# Revit family: M186140xx--Sanitary_Shower-screens_Roca_VICTORIA-L2-E-1400-Front-shower-enclosure-with-1-sliding-door-+-1-fixed-panel
name_source: partatom
category: Specialty Equipment
units: mm (PartAtom-declared; Revit-internal decimal feet)

## family parameters
Always vertical = No
Cut with Voids When Loaded = No
OmniClass Number = 23.31.17.25
Part Type = Normal
Room Calculation Point = No
Round Connector Dimension = Use Diameter
Shared = No
Work Plane-Based = No

## types (1)
- VICTORIA L2-E 1400 - Front shower enclosure with 1 sliding door + 1 fixed panel
    Always visible = Yes
    BIMobject category = Shower screens
    Design country = Spain
    Edition number = 1
    Frame material = Roca - VICTORIA - Polished silver
    IFC Classification = Wall
    Installation instructions = http://www.export.roca.com
    Manufacturer = Roca
    Manufacturer country = Spain
    Manufacturer name = Roca
    Masterformat 2014 Code = 10 28 19.16
    Masterformat 2014 Description = Shower Doors
    Material main = Glass
    Material secondary = Aluminium
    Model = VICTORIA L2-E 1400 - Front shower enclosure with 1 sliding door + 1 fixed panel
    NBS Reference Code = 35-06-79
    NBS Reference Description = Shower Enclosures
    OmniClass Code = 23-31 17 25
    OmniClass Description = Shower Screens
    Panel material = Roca - VICTORIA - 12 Clear glass
    Product Guid = 346a807e-4b01-4754-9fe7-ba9d0cd4c0e3
    Product SKU = M186140xx
    Product data url = https://www.bimobject.com
    Product family = Victoria
    Product group = Shower screen
    Product name = VICTORIA L2-E 1400 - Front shower enclosure with 1 sliding door + 1 fixed panel
    Product url = http://www.export.roca.com
    QR code = https://www.roca.com
    Technical description = http://www.export.roca.com
    UNSPSC Code = 30181507
    URL = http://www.roca.com
    Uniclass 2015 Code = Pr_40_20_06_79
    Uniclass 2015 Name = Shower enclosures
    Uniformat II Code = E2010
    Uniformat II Description = Fixed Furnishings
    Youtube clip = https://www.youtube.com

## geometry (parser evidence)
native form markers: Blend x4, Sweep x2
no freeform markers — native parametric forms only
